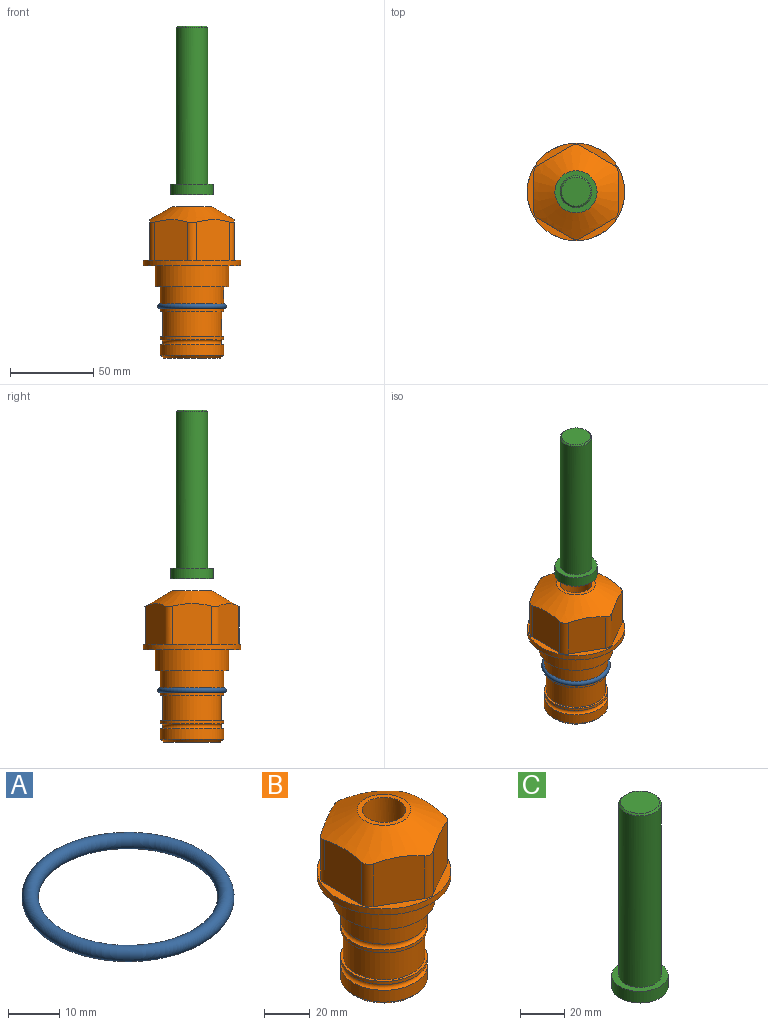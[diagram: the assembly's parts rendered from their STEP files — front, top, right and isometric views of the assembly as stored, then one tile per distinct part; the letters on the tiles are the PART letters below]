
ASSEMBLY  parts=3 mates=1
PART A: 1 faces, bbox 44.7x44.7x3.2 mm
  f0: torus R=19.05mm, axis (0,0,1), area 1193.9mm2
PART B: 36 faces, bbox 58.7x58.7x91.2 mm
  f0: cylinder r=17.78mm len=35.56mm, axis (0,0,1), area 1670.8mm2, adj f23,f24,f31
  f1: cylinder r=19.05mm len=38.1mm, axis (0,0,1), area 1191.9mm2, adj f26,f27,f30
  f2: plane 58.66x58.66mm, normal (0,0,-1), area 1150.6mm2, adj f3,f28
  f3: cylinder r=29.33mm len=58.66mm, axis (0,0,-1), area 585.1mm2, adj f2,f4
  f4: plane 58.66x58.66mm, normal (0,0,1), area 475.9mm2, adj f3,f5,f6,f7,f8,f9,f10,f11
  f5: plane 24.5x20.32mm, normal (-0.5,0.87,0), area 562.8mm2, adj f4,f15,f16,f17
  f6: plane 24.5x20.32mm, normal (0.5,0.87,0), area 562.8mm2, adj f4,f14,f15,f17
  f7: plane 24.5x23.48mm, normal (1,0,0), area 562.8mm2, adj f4,f13,f14,f17
  f8: plane 24.5x20.32mm, normal (0.5,-0.87,0), area 562.8mm2, adj f4,f12,f13,f17
  f9: plane 24.5x20.32mm, normal (-0.5,-0.87,0), area 562.8mm2, adj f4,f11,f12,f17
  f10: plane 24.5x23.48mm, normal (-1,0,0), area 562.8mm2, adj f4,f11,f16,f17
  f11: cylinder r=5.08mm len=23.01mm, axis (0,0,-1), area 121.2mm2, adj f4,f9,f10,f17
  f12: cylinder r=5.08mm len=23.01mm, axis (0,0,-1), area 121.2mm2, adj f4,f8,f9,f17
  f13: cylinder r=5.08mm len=23.01mm, axis (0,0,-1), area 121.2mm2, adj f4,f7,f8,f17
  f14: cylinder r=5.08mm len=23.01mm, axis (0,0,-1), area 121.2mm2, adj f4,f6,f7,f17
  f15: cylinder r=5.08mm len=23.01mm, axis (0,0,-1), area 121.2mm2, adj f4,f5,f6,f17
  f16: cylinder r=5.08mm len=23.01mm, axis (0,0,-1), area 121.2mm2, adj f4,f5,f10,f17
  f17: cone r=11.73mm half-angle=60deg, axis (0,0,-1), area 2071.8mm2, adj f5,f6,f7,f8,f9,f10,f11,f12
  f18: plane 23.46x23.46mm, normal (0,0,1), area 147.4mm2, adj f17,f35
  f19: plane 34.93x34.93mm, normal (0,0,-1), area 958mm2, adj f29
  f20: cylinder r=19.05mm len=38.1mm, axis (0,0,1), area 760.1mm2, adj f21,f29
  f21: torus R=19.05mm, axis (0,0,1), area 565.3mm2, adj f20,f22
  f22: cylinder r=19.05mm len=38.1mm, axis (0,0,1), area 190mm2, adj f21,f23
  f23: plane 38.1x38.1mm, normal (0,0,1), area 146.9mm2, adj f0,f22
  f24: plane 38.1x38.1mm, normal (0,0,-1), area 146.9mm2, adj f0,f25
  f25: cylinder r=19.05mm len=38.1mm, axis (0,0,1), area 190mm2, adj f24,f26
  f26: torus R=19.05mm, axis (0,0,1), area 565.3mm2, adj f1,f25
  f27: plane 44.45x44.45mm, normal (0,0,-1), area 411.7mm2, adj f1,f28
  f28: cylinder r=22.23mm len=44.45mm, axis (0,0,1), area 1773.5mm2, adj f2,f27
  f29: cone r=19.05mm half-angle=45deg, axis (0,0,1), area 257.5mm2, adj f19,f20
  f30: cylinder r=3.17mm len=6.75mm, axis (-1,0,0), area 128mm2, adj f1,f33
  f31: cylinder r=3.17mm len=6.35mm, axis (-1,0,0), area 102.5mm2, adj f0,f33
  f32: plane 25.4x25.4mm, normal (0,0,1), area 506.7mm2, adj f33
  f33: cylinder r=12.7mm len=66.42mm, axis (0,0,-1), area 5236.2mm2, adj f30,f31,f32,f34
  f34: cone r=9.53mm half-angle=30deg, axis (0,0,-1), area 443.4mm2, adj f33,f35
  f35: cylinder r=9.53mm len=19.05mm, axis (0,0,-1), area 849mm2, adj f18,f34
PART C: 6 faces, bbox 25.4x25.4x101.6 mm
  f0: plane 17.46x17.46mm, normal (0,0,1), area 239.5mm2, adj f5
  f1: plane 25.4x25.4mm, normal (0,0,-1), area 506.7mm2, adj f2
  f2: cylinder r=12.7mm len=25.4mm, axis (0,0,1), area 506.7mm2, adj f1,f3
  f3: plane 25.4x25.4mm, normal (0,0,1), area 221.7mm2, adj f2,f4
  f4: cylinder r=9.53mm len=94.46mm, axis (0,0,1), area 5653mm2, adj f3,f5
  f5: cone r=8.73mm half-angle=45deg, axis (0,0,-1), area 64.4mm2, adj f0,f4
PLACE A at identity
PLACE B at identity fixed
PLACE C rot(axis=(0,0,1),36.8deg) t=(0,0,70.54)mm
MATE cylindrical C.f2 <-> B.f0  axis (0,0,1) through (0,0,96.18)mm
